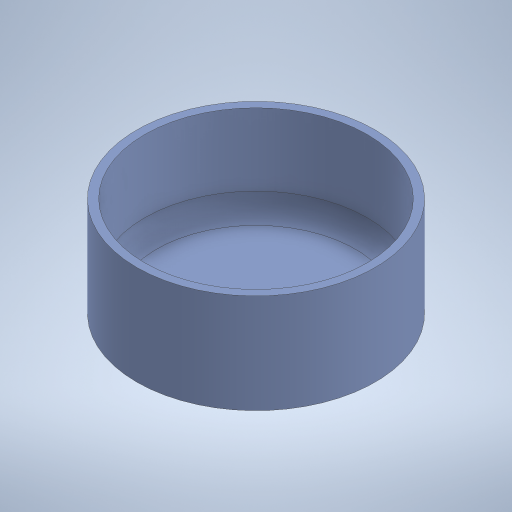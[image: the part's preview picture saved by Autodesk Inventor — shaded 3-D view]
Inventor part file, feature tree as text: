
AUTODESK INVENTOR PART (.ipt)
format: ipt  version: 2024 (Build 280153020, 153B)  size: 245,760 bytes
history: native  units: mm
features: sketch x2, revolve x1, extrude x1
ambient origin geometry x8: Origin, YZ Plane, XZ Plane, XY Plane, X Axis, Y Axis, Z Axis, Center Point
bodies: Solid1 (feature_tree)
feature tree (4):
  revolve  "Revolution1"  [1 undecoded]
  extrude  "Extrusion1"  Depth=25.0mm
  sketch  "Sketch1"  dims[d2=1.5mm d6=25.0mm]
  sketch  "Sketch3"  dims[d8=30.0mm d20=25.0mm d21=2.0mm d22=5.0mm d23=180.0deg d24=180.0deg d25=6.8mm d26=10.0mm d27=0.0mm d15=0.872665mm d16=0.872665mm]
note: 1 required parameter value undecoded (feature->parameter linkage not recoverable at this tier; creation-order binding heuristic only, values carry confidence <= 0.55)
